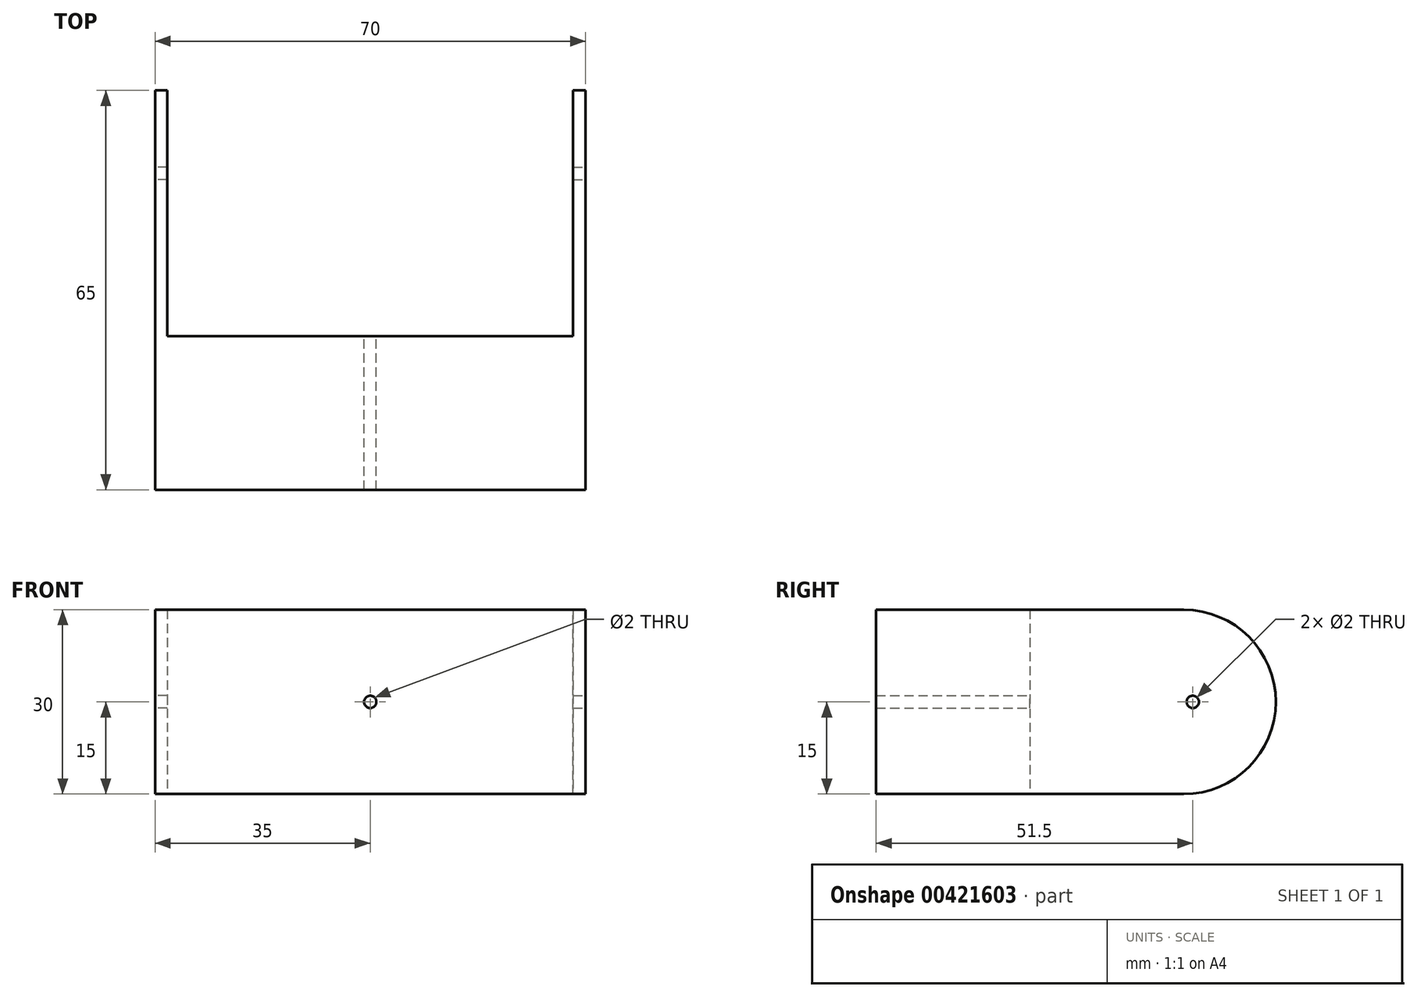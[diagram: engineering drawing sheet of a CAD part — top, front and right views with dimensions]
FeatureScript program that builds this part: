
annotation { "Feature Type Name" : "Feature", "Feature Type Description" : "" }
export const myFeature = defineFeature(function(context is Context, id is Id, definition is map)
    precondition{}
    {
        {
            var Q0;
            Q0=qCreatedBy(makeId("Front.planeOp"),FACE);
            var sketch = newSketch(context, id + "F0", { "sketchPlane" : qUnion([Q0])});
            skLineSegment(sketch, "E0.bottom", {"start": v(35, 15) * mm, "end": v(-35, 15) * mm});
            skLineSegment(sketch, "E0.top", {"start": v(35, -15) * mm, "end": v(-35, -15) * mm});
            skLineSegment(sketch, "E0.left", {"start": v(35, 15) * mm, "end": v(35, -15) * mm});
            skLineSegment(sketch, "E0.right", {"start": v(-35, 15) * mm, "end": v(-35, -15) * mm});
            skPoint(sketch, "E0.middle", {"position": v(0, 0) * mm});
            skPoint(sketch, "E1.endSnap0", {"position": v(0, -15) * mm});
            skCircle(sketch, "E2", {"center": v(0, 0) * mm, "radius": 1 * mm});
            skLineSegment(sketch, "E3", {"start": v(33, 15) * mm, "end": v(33, -15) * mm});
            skLineSegment(sketch, "E4", {"start": v(-33, 15) * mm, "end": v(-33, -15) * mm});
            skSolve(sketch);
        }
        {
            var Q0;
            {var subQ0=sQuery(id+"F0.wireOp",EDGE,"E0.right");var subQ1=sQuery(id+"F0.wireOp",EDGE,"E0.top");var subQ2=makeQuery(id+"F0.imprint","INTERSECT",VERTEX,{"derivedFrom":[subQ1,subQ0]});Q0=makeQuery(id+"F0.imprint","IMPRINT",FACE,{"disambiguationData":[TD([[makeQuery(id+"F0.imprint","IMPRINT",EDGE,{"disambiguationData":[TD([[subQ2,1.0]])],"derivedFrom":subQ1}),-1.0]])]});}
            var Q1;
            {var subQ3=sQuery(id+"F0.wireOp",EDGE,"tDa7KL4P-Mlag-EH9R-2iVy-iCjy4LGFu3fu");Q1=makeQuery(id+"F0.imprint","IMPRINT",FACE,{"disambiguationData":[TD([[makeQuery(id+"F0.imprint","IMPRINT",EDGE,{"derivedFrom":subQ3}),-1.0]])]});}
            var Q2;
            {var subQ0=sQuery(id+"F0.wireOp",EDGE,"E0.left");var subQ1=sQuery(id+"F0.wireOp",EDGE,"E0.top");var subQ2=makeQuery(id+"F0.imprint","INTERSECT",VERTEX,{"derivedFrom":[subQ1,subQ0]});Q2=makeQuery(id+"F0.imprint","IMPRINT",FACE,{"disambiguationData":[TD([[makeQuery(id+"F0.imprint","IMPRINT",EDGE,{"disambiguationData":[TD([[subQ2,-1.0]])],"derivedFrom":subQ1}),-1.0]])]});}
            var Q3;
            {var subQ3=sQuery(id+"F0.wireOp",EDGE,"htGaxIO0-QAEM-4Pdc-kALO-n7SKx8bL2aY7");Q3=makeQuery(id+"F0.imprint","IMPRINT",FACE,{"disambiguationData":[TD([[makeQuery(id+"F0.imprint","IMPRINT",EDGE,{"derivedFrom":subQ3}),1.0]])]});}
            var Q4;
            {var subQ9=sQuery(id+"F0.wireOp",EDGE,"tDa7KL4P-Mlag-EH9R-2iVy-iCjy4LGFu3fu");Q4=makeQuery(id+"F0.imprint","IMPRINT",FACE,{"disambiguationData":[TD([[makeQuery(id+"F0.imprint","IMPRINT",EDGE,{"derivedFrom":subQ9}),1.0]])]});}
            var Q5;
            Q5=makeQuery(id+"F0.imprint","IMPRINT",FACE,{"disambiguationData":[TD([[makeQuery(id+"F0.imprint","IMPRINT",EDGE,{"derivedFrom":sQuery(id+"F0.wireOp",EDGE,"oupXBTgc-YdYU-vdsE-jyIt-t6NzdKqYyRsU")}),-1.0]])]});
            var Q6;
            {var subQ5=sQuery(id+"F0.wireOp",EDGE,"HhFWCQhV-jva5-64Ox-B1Ob-24eSKecyCGVs.bottom");Q6=makeQuery(id+"F0.imprint","IMPRINT",FACE,{"disambiguationData":[TD([[makeQuery(id+"F0.imprint","IMPRINT",EDGE,{"derivedFrom":subQ5}),1.0]])]});}
            var Q7;
            {var subQ5=sQuery(id+"F0.wireOp",EDGE,"95491e5b-2522-43dd-8094-d442577f57930.MirrorCS");Q7=makeQuery(id+"F0.imprint","IMPRINT",FACE,{"disambiguationData":[TD([[makeQuery(id+"F0.imprint","IMPRINT",EDGE,{"derivedFrom":subQ5}),-1.0]])]});}
            var Q8;
            Q8=makeQuery(id+"F0.imprint","IMPRINT",FACE,{"disambiguationData":[TD([[makeQuery(id+"F0.imprint","IMPRINT",EDGE,{"derivedFrom":sQuery(id+"F0.wireOp",EDGE,"oupXBTgc-YdYU-vdsE-jyIt-t6NzdKqYyRsU")}),1.0]])]});
            var Q9;
            {var subQ0=sQuery(id+"F0.wireOp",EDGE,"rNfMHuuz-hu2V-mA34-Ymti-NQEB7Dtc70eJ");var subQ1=sQuery(id+"F0.wireOp",EDGE,"eWT2dNut-7A9A-fftn-m84f-pIBRwlpAPyBL");var subQ2=makeQuery(id+"F0.imprint","INTERSECT",VERTEX,{"derivedFrom":[subQ1,subQ0]});Q9=makeQuery(id+"F0.imprint","IMPRINT",FACE,{"disambiguationData":[TD([[makeQuery(id+"F0.imprint","IMPRINT",EDGE,{"disambiguationData":[TD([[subQ2,-1.0]])],"derivedFrom":subQ1}),1.0]])]});}
            var Q10;
            {var subQ4=sQuery(id+"F0.wireOp",EDGE,"E0.bottom");var subQ6=sQuery(id+"F0.wireOp",EDGE,"E0.right");var subQ7=makeQuery(id+"F0.imprint","INTERSECT",VERTEX,{"derivedFrom":[subQ4,subQ6]});Q10=makeQuery(id+"F0.imprint","IMPRINT",FACE,{"disambiguationData":[TD([[makeQuery(id+"F0.imprint","IMPRINT",EDGE,{"disambiguationData":[TD([[subQ7,1.0]])],"derivedFrom":subQ4}),1.0]])]});}
            var Q11;
            {var subQ0=sQuery(id+"F0.wireOp",EDGE,"HhFWCQhV-jva5-64Ox-B1Ob-24eSKecyCGVs.right");var subQ1=sQuery(id+"F0.wireOp",EDGE,"EY7JK4PB-J7if-fDYU-2uPh-CaVDfb0bhEIO");var subQ2=makeQuery(id+"F0.imprint","INTERSECT",VERTEX,{"derivedFrom":[subQ1,subQ0]});Q11=makeQuery(id+"F0.imprint","IMPRINT",FACE,{"disambiguationData":[TD([[makeQuery(id+"F0.imprint","IMPRINT",EDGE,{"disambiguationData":[TD([[subQ2,-1.0]])],"derivedFrom":subQ1}),-1.0]])]});}
            var Q12;
            {var subQ0=sQuery(id+"F0.wireOp",EDGE,"rNfMHuuz-hu2V-mA34-Ymti-NQEB7Dtc70eJ");var subQ1=sQuery(id+"F0.wireOp",EDGE,"89ed316c-a835-4cf1-a14d-9285fc2a6e7f0.MirrorCS");var subQ2=makeQuery(id+"F0.imprint","INTERSECT",VERTEX,{"derivedFrom":[subQ1,subQ0]});Q12=makeQuery(id+"F0.imprint","IMPRINT",FACE,{"disambiguationData":[TD([[makeQuery(id+"F0.imprint","IMPRINT",EDGE,{"disambiguationData":[TD([[subQ2,-1.0]])],"derivedFrom":subQ1}),-1.0]])]});}
            var Q13;
            {var subQ0=sQuery(id+"F0.wireOp",EDGE,"0ba24afe-1459-484d-81cf-bf17d9db052f0.MirrorCS");var subQ1=sQuery(id+"F0.wireOp",EDGE,"RjKb90H9-plP9-b85y-cHrJ-WinZ8lQvUb3o");var subQ2=makeQuery(id+"F0.imprint","INTERSECT",VERTEX,{"derivedFrom":[subQ1,subQ0]});Q13=makeQuery(id+"F0.imprint","IMPRINT",FACE,{"disambiguationData":[TD([[makeQuery(id+"F0.imprint","IMPRINT",EDGE,{"disambiguationData":[TD([[subQ2,-1.0]])],"derivedFrom":subQ1}),1.0]])]});}
            var Q14;
            {var subQ4=sQuery(id+"F0.wireOp",EDGE,"E0.bottom");var subQ6=sQuery(id+"F0.wireOp",EDGE,"E0.left");var subQ7=makeQuery(id+"F0.imprint","INTERSECT",VERTEX,{"derivedFrom":[subQ4,subQ6]});Q14=makeQuery(id+"F0.imprint","IMPRINT",FACE,{"disambiguationData":[TD([[makeQuery(id+"F0.imprint","IMPRINT",EDGE,{"disambiguationData":[TD([[subQ7,-1.0]])],"derivedFrom":subQ4}),1.0]])]});}
            var Q15;
            {var subQ0=sQuery(id+"F0.wireOp",EDGE,"89ed316c-a835-4cf1-a14d-9285fc2a6e7f0.MirrorCS");var subQ1=sQuery(id+"F0.wireOp",EDGE,"E0.bottom");var subQ2=makeQuery(id+"F0.imprint","INTERSECT",VERTEX,{"derivedFrom":[subQ1,subQ0]});Q15=makeQuery(id+"F0.imprint","IMPRINT",FACE,{"disambiguationData":[TD([[makeQuery(id+"F0.imprint","IMPRINT",EDGE,{"disambiguationData":[TD([[subQ2,-1.0]])],"derivedFrom":subQ1}),1.0]])]});}
            var Q16;
            {var subQ0=sQuery(id+"F0.wireOp",EDGE,"0ba24afe-1459-484d-81cf-bf17d9db052f0.MirrorCS");var subQ1=sQuery(id+"F0.wireOp",EDGE,"E0.bottom");var subQ2=makeQuery(id+"F0.imprint","INTERSECT",VERTEX,{"derivedFrom":[subQ1,subQ0]});Q16=makeQuery(id+"F0.imprint","IMPRINT",FACE,{"disambiguationData":[TD([[makeQuery(id+"F0.imprint","IMPRINT",EDGE,{"disambiguationData":[TD([[subQ2,1.0]])],"derivedFrom":subQ1}),1.0]])]});}
            var Q17;
            {var subQ0=sQuery(id+"F0.wireOp",EDGE,"HhFWCQhV-jva5-64Ox-B1Ob-24eSKecyCGVs.right");var subQ5=sQuery(id+"F0.wireOp",EDGE,"rNfMHuuz-hu2V-mA34-Ymti-NQEB7Dtc70eJ");var subQ6=makeQuery(id+"F0.imprint","INTERSECT",VERTEX,{"derivedFrom":[subQ5,subQ0]});Q17=makeQuery(id+"F0.imprint","IMPRINT",FACE,{"disambiguationData":[TD([[makeQuery(id+"F0.imprint","IMPRINT",EDGE,{"disambiguationData":[TD([[subQ6,-1.0]])],"derivedFrom":subQ5}),1.0]])]});}
            var Q18;
            {var subQ0=sQuery(id+"F0.wireOp",EDGE,"eWT2dNut-7A9A-fftn-m84f-pIBRwlpAPyBL");var subQ1=sQuery(id+"F0.wireOp",EDGE,"E0.bottom");var subQ2=makeQuery(id+"F0.imprint","INTERSECT",VERTEX,{"derivedFrom":[subQ1,subQ0]});Q18=makeQuery(id+"F0.imprint","IMPRINT",FACE,{"disambiguationData":[TD([[makeQuery(id+"F0.imprint","IMPRINT",EDGE,{"disambiguationData":[TD([[subQ2,-1.0]])],"derivedFrom":subQ0}),1.0]])]});}
            var Q19;
            {var subQ5=sQuery(id+"F0.wireOp",EDGE,"HhFWCQhV-jva5-64Ox-B1Ob-24eSKecyCGVs.top");Q19=makeQuery(id+"F0.imprint","IMPRINT",FACE,{"disambiguationData":[TD([[makeQuery(id+"F0.imprint","IMPRINT",EDGE,{"derivedFrom":subQ5}),-1.0]])]});}
            var Q20;
            Q20=makeQuery(id+"F0.imprint","IMPRINT",FACE,{"disambiguationData":[TD([[makeQuery(id+"F0.imprint","IMPRINT",EDGE,{"derivedFrom":sQuery(id+"F0.wireOp",EDGE,"E2")}),-1.0]])]});
            extrude(context, id + "F1", {"entities" : qUnion([Q0, Q1, Q2, Q3, Q4, Q5, Q6, Q7, Q8, Q9, Q10, Q11, Q12, Q13, Q14, Q15, Q16, Q17, Q18, Q19, Q20]), "depth" : 25 * mm});
        }
        {
            var Q0;
            {var subQ0=sQuery(id+"F0.wireOp",EDGE,"E0.left");Q0=makeQuery(id+"F0.imprint","IMPRINT",FACE,{"disambiguationData":[TD([[makeQuery(id+"F0.imprint","IMPRINT",EDGE,{"derivedFrom":subQ0}),-1.0]])]});}
            var Q1;
            {var subQ0=sQuery(id+"F0.wireOp",EDGE,"E0.right");Q1=makeQuery(id+"F0.imprint","IMPRINT",FACE,{"disambiguationData":[TD([[makeQuery(id+"F0.imprint","IMPRINT",EDGE,{"derivedFrom":subQ0}),1.0]])]});}
            var Q2;
            {var subQ5=sQuery(id+"F0.wireOp",EDGE,"rNfMHuuz-hu2V-mA34-Ymti-NQEB7Dtc70eJ");Q2=makeQuery(id+"F0.imprint","IMPRINT",FACE,{"disambiguationData":[TD([[makeQuery(id+"F0.imprint","IMPRINT",EDGE,{"derivedFrom":subQ5}),1.0]])]});}
            var Q3;
            {var subQ4=sQuery(id+"F0.wireOp",EDGE,"E0.right");var subQ5=sQuery(id+"F0.wireOp",EDGE,"E0.bottom");var subQ6=makeQuery(id+"F0.imprint","INTERSECT",VERTEX,{"derivedFrom":[subQ5,subQ4]});Q3=makeQuery(id+"F0.imprint","IMPRINT",FACE,{"disambiguationData":[TD([[makeQuery(id+"F0.imprint","IMPRINT",EDGE,{"disambiguationData":[TD([[subQ6,1.0]])],"derivedFrom":subQ5}),1.0]])]});}
            var Q4;
            {var subQ4=sQuery(id+"F0.wireOp",EDGE,"E0.left");var subQ5=sQuery(id+"F0.wireOp",EDGE,"E0.bottom");var subQ6=makeQuery(id+"F0.imprint","INTERSECT",VERTEX,{"derivedFrom":[subQ5,subQ4]});Q4=makeQuery(id+"F0.imprint","IMPRINT",FACE,{"disambiguationData":[TD([[makeQuery(id+"F0.imprint","IMPRINT",EDGE,{"disambiguationData":[TD([[subQ6,-1.0]])],"derivedFrom":subQ5}),1.0]])]});}
            extrude(context, id + "F2", {"entities" : qUnion([Q0, Q1, Q2, Q3, Q4]), "operationType" : NewBodyOperationType.ADD, "oppositeDirection" : true, "depth" : 25 * mm});
        }
        {
            var Q0;
            {var subQ0=sQuery(id+"F0.wireOp",EDGE,"E0.left");Q0=makeQuery(id+"F2.boolean.opBoolean","MERGE",FACE,{"derivedFrom":[makeQuery(id+"F1.opExtrude","SWEPT_FACE",FACE,{"disambiguationData":[OSD([subQ0])]}),makeQuery(id+"F2.opExtrude","SWEPT_FACE",FACE,{"disambiguationData":[OSD([subQ0])]})]});}
            var sketch = newSketch(context, id + "F3", { "sketchPlane" : qUnion([Q0])});
            skArc(sketch, "E5", {"start": v(25, -15) * mm, "mid": v(40, 0) * mm, "end": v(25, 15) * mm});
            skCircle(sketch, "E6", {"center": v(26.5, 0) * mm, "radius": 1 * mm});
            skSolve(sketch);
        }
        {
            var Q0;
            Q0=makeQuery(id+"F3.imprint","IMPRINT",FACE,{"disambiguationData":[TD([[makeQuery(id+"F3.imprint","IMPRINT",EDGE,{"derivedFrom":sQuery(id+"F3.wireOp",EDGE,"E5")}),1.0]])]});
            extrude(context, id + "F4", {"entities" : qUnion([Q0]), "operationType" : NewBodyOperationType.ADD, "oppositeDirection" : true, "depth" : 2 * mm});
        }
        {
            var Q0;
            {var subQ0=sQuery(id+"F0.wireOp",EDGE,"E0.right");Q0=makeQuery(id+"F2.boolean.opBoolean","MERGE",FACE,{"derivedFrom":[makeQuery(id+"F1.opExtrude","SWEPT_FACE",FACE,{"disambiguationData":[OSD([subQ0])]}),makeQuery(id+"F2.opExtrude","SWEPT_FACE",FACE,{"disambiguationData":[OSD([subQ0])]})]});}
            var sketch = newSketch(context, id + "F5", { "sketchPlane" : qUnion([Q0])});
            skArc(sketch, "E7", {"start": v(-25, 15) * mm, "mid": v(-40, 0) * mm, "end": v(-25, -15) * mm});
            skCircle(sketch, "E8", {"center": v(-26.5, 0) * mm, "radius": 1 * mm});
            skSolve(sketch);
        }
        {
            var Q0;
            Q0=makeQuery(id+"F5.imprint","IMPRINT",FACE,{"disambiguationData":[TD([[makeQuery(id+"F5.imprint","IMPRINT",EDGE,{"derivedFrom":sQuery(id+"F5.wireOp",EDGE,"E7")}),1.0]])]});
            extrude(context, id + "F6", {"entities" : qUnion([Q0]), "operationType" : NewBodyOperationType.ADD, "oppositeDirection" : true, "depth" : 2 * mm});
        }
    });
